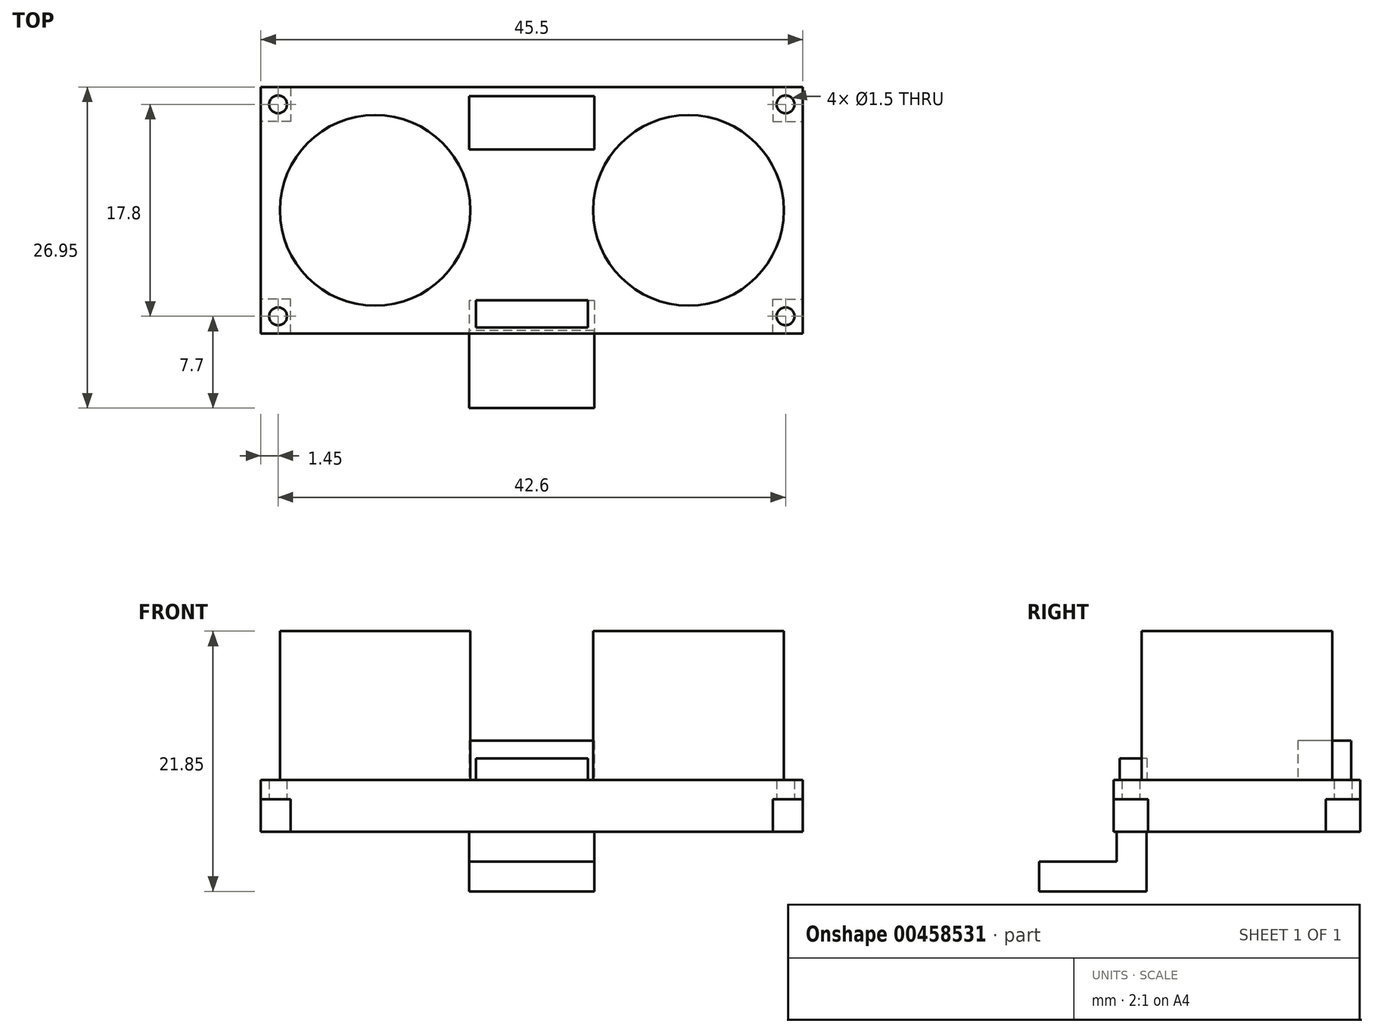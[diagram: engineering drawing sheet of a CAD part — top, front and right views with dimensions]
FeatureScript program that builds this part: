
annotation { "Feature Type Name" : "Feature", "Feature Type Description" : "" }
export const myFeature = defineFeature(function(context is Context, id is Id, definition is map)
    precondition{}
    {
        {
            var Q0;
            Q0=qCreatedBy(makeId("Top.planeOp"),FACE);
            var sketch = newSketch(context, id + "F0", { "sketchPlane" : qUnion([Q0])});
            skLineSegment(sketch, "E0.bottom", {"start": v(-22.75, 10.35) * mm, "end": v(22.75, 10.35) * mm});
            skLineSegment(sketch, "E0.top", {"start": v(-22.75, -10.35) * mm, "end": v(22.75, -10.35) * mm});
            skLineSegment(sketch, "E0.left", {"start": v(-22.75, 10.35) * mm, "end": v(-22.75, -10.35) * mm});
            skLineSegment(sketch, "E0.right", {"start": v(22.75, 10.35) * mm, "end": v(22.75, -10.35) * mm});
            skPoint(sketch, "E0.middle", {"position": v(0, 0) * mm});
            skCircle(sketch, "E1", {"center": v(-21.3, 8.9) * mm, "radius": 0.75 * mm});
            skCircle(sketch, "E2.MirrorC", {"center": v(21.3, 8.9) * mm, "radius": 0.75 * mm});
            skCircle(sketch, "E3.MirrorC", {"center": v(21.3, -8.9) * mm, "radius": 0.75 * mm});
            skCircle(sketch, "E4.MirrorC", {"center": v(-21.3, -8.9) * mm, "radius": 0.75 * mm});
            skSolve(sketch);
        }
        {
            var Q0;
            Q0=qSketchRegion(id+"F0",true);
            extrude(context, id + "F1", {"entities" : qUnion([Q0]), "depth" : 1.6 * mm});
        }
        {
            var Q0;
            Q0=makeQuery(id+"F1.opExtrude","CAP_FACE",FACE,{"disambiguationData":[OSD([sQuery(id+"F0.wireOp",EDGE,"E0.bottom"),sQuery(id+"F0.wireOp",EDGE,"E0.top"),sQuery(id+"F0.wireOp",EDGE,"E0.left"),sQuery(id+"F0.wireOp",EDGE,"E0.right"),sQuery(id+"F0.wireOp",EDGE,"E1"),sQuery(id+"F0.wireOp",EDGE,"E2.MirrorC"),sQuery(id+"F0.wireOp",EDGE,"E3.MirrorC"),sQuery(id+"F0.wireOp",EDGE,"E4.MirrorC"),sQuery(id+"F0.wireOp",EDGE,"EcKcbucg-EIJj-1O6K-RH2d-xdvmN5E1ucRb"),sQuery(id+"F0.wireOp",EDGE,"HiSo9sqT-VgG6-14Ua-RjyV-KtrsNFatjuRK")])],"isStart":false});
            var sketch = newSketch(context, id + "F2", { "sketchPlane" : qUnion([Q0])});
            skCircle(sketch, "E5", {"center": v(-13.15, 0) * mm, "radius": 8 * mm});
            skCircle(sketch, "E6", {"center": v(13.15, 0) * mm, "radius": 8 * mm});
            skLineSegment(sketch, "E7.bottom", {"start": v(-5.25, 9.6) * mm, "end": v(5.25, 9.6) * mm});
            skLineSegment(sketch, "E7.top", {"start": v(-5.25, 5.1) * mm, "end": v(5.25, 5.1) * mm});
            skLineSegment(sketch, "E7.left", {"start": v(-5.25, 9.6) * mm, "end": v(-5.25, 5.1) * mm});
            skLineSegment(sketch, "E7.right", {"start": v(5.25, 9.6) * mm, "end": v(5.25, 5.1) * mm});
            skPoint(sketch, "E7.middle", {"position": v(0, 7.35) * mm});
            skLineSegment(sketch, "E8.bottom", {"start": v(-4.7, -7.55) * mm, "end": v(4.7, -7.55) * mm});
            skLineSegment(sketch, "E8.top", {"start": v(-4.7, -9.85) * mm, "end": v(4.7, -9.85) * mm});
            skLineSegment(sketch, "E8.left", {"start": v(-4.7, -7.55) * mm, "end": v(-4.7, -9.85) * mm});
            skLineSegment(sketch, "E8.right", {"start": v(4.7, -7.55) * mm, "end": v(4.7, -9.85) * mm});
            skPoint(sketch, "E8.middle", {"position": v(0, -8.7) * mm});
            skSolve(sketch);
        }
        {
            var Q0;
            Q0=makeQuery(id+"F2.imprint","IMPRINT",FACE,{"disambiguationData":[TD([[makeQuery(id+"F2.imprint","IMPRINT",EDGE,{"derivedFrom":sQuery(id+"F2.wireOp",EDGE,"E5")}),1.0]])]});
            var Q1;
            Q1=makeQuery(id+"F2.imprint","IMPRINT",FACE,{"disambiguationData":[TD([[makeQuery(id+"F2.imprint","IMPRINT",EDGE,{"derivedFrom":sQuery(id+"F2.wireOp",EDGE,"E6")}),1.0]])]});
            extrude(context, id + "F3", {"entities" : qUnion([Q0, Q1]), "operationType" : NewBodyOperationType.ADD, "depth" : 12.5 * mm});
        }
        {
            var Q0;
            Q0=makeQuery(id+"F2.imprint","IMPRINT",FACE,{"disambiguationData":[TD([[makeQuery(id+"F2.imprint","IMPRINT",EDGE,{"derivedFrom":sQuery(id+"F2.wireOp",EDGE,"E7.bottom")}),-1.0]])]});
            extrude(context, id + "F4", {"entities" : qUnion([Q0]), "operationType" : NewBodyOperationType.ADD, "depth" : 3.3 * mm});
        }
        {
            var Q0;
            Q0=makeQuery(id+"F2.imprint","IMPRINT",FACE,{"disambiguationData":[TD([[makeQuery(id+"F2.imprint","IMPRINT",EDGE,{"derivedFrom":sQuery(id+"F2.wireOp",EDGE,"E8.bottom")}),-1.0]])]});
            extrude(context, id + "F5", {"entities" : qUnion([Q0]), "operationType" : NewBodyOperationType.ADD, "depth" : 1.8 * mm});
        }
        {
            var Q0;
            Q0=makeQuery(id+"F1.opExtrude","CAP_FACE",FACE,{"disambiguationData":[OSD([sQuery(id+"F0.wireOp",EDGE,"E0.bottom"),sQuery(id+"F0.wireOp",EDGE,"E0.top"),sQuery(id+"F0.wireOp",EDGE,"E0.left"),sQuery(id+"F0.wireOp",EDGE,"E0.right"),sQuery(id+"F0.wireOp",EDGE,"E1"),sQuery(id+"F0.wireOp",EDGE,"E2.MirrorC"),sQuery(id+"F0.wireOp",EDGE,"E3.MirrorC"),sQuery(id+"F0.wireOp",EDGE,"E4.MirrorC")])],"isStart":true});
            var sketch = newSketch(context, id + "F6", { "sketchPlane" : qUnion([Q0])});
            skLineSegment(sketch, "E9", {"start": v(-20.25, -10.35) * mm, "end": v(-20.25, -7.45) * mm});
            skLineSegment(sketch, "E10", {"start": v(-20.25, -7.45) * mm, "end": v(-22.75, -7.45) * mm});
            skLineSegment(sketch, "E11.MirrorCS", {"start": v(-20.25, 7.45) * mm, "end": v(-22.75, 7.45) * mm});
            skLineSegment(sketch, "E12.MirrorCS", {"start": v(-20.25, 10.35) * mm, "end": v(-20.25, 7.45) * mm});
            skLineSegment(sketch, "E13.MirrorCS", {"start": v(20.25, 10.35) * mm, "end": v(20.25, 7.45) * mm});
            skLineSegment(sketch, "E14.MirrorCS", {"start": v(20.25, 7.45) * mm, "end": v(22.75, 7.45) * mm});
            skLineSegment(sketch, "E15.MirrorCS", {"start": v(20.25, -10.35) * mm, "end": v(20.25, -7.45) * mm});
            skLineSegment(sketch, "E16.MirrorCS", {"start": v(20.25, -7.45) * mm, "end": v(22.75, -7.45) * mm});
            skSolve(sketch);
        }
        {
            var Q0;
            {var subQ6=sQuery(id+"F6.wireOp",EDGE,"E9");Q0=makeQuery(id+"F6.imprint","IMPRINT",FACE,{"disambiguationData":[TD([[makeQuery(id+"F6.imprint","IMPRINT",EDGE,{"derivedFrom":subQ6}),-1.0]])]});}
            extrude(context, id + "F7", {"entities" : qUnion([Q0]), "operationType" : NewBodyOperationType.ADD, "depth" : 2.75 * mm});
        }
        {
            var Q0;
            Q0=makeQuery(id+"F7.opExtrude","CAP_FACE",FACE,{"disambiguationData":[OSD([sQuery(id+"F0.wireOp",EDGE,"E0.bottom"),sQuery(id+"F0.wireOp",EDGE,"E0.top"),sQuery(id+"F0.wireOp",EDGE,"E0.left"),sQuery(id+"F0.wireOp",EDGE,"E0.right"),sQuery(id+"F6.wireOp",EDGE,"E9"),sQuery(id+"F6.wireOp",EDGE,"E10"),sQuery(id+"F6.wireOp",EDGE,"E11.MirrorCS"),sQuery(id+"F6.wireOp",EDGE,"E12.MirrorCS"),sQuery(id+"F6.wireOp",EDGE,"E13.MirrorCS"),sQuery(id+"F6.wireOp",EDGE,"E14.MirrorCS"),sQuery(id+"F6.wireOp",EDGE,"E15.MirrorCS"),sQuery(id+"F6.wireOp",EDGE,"E16.MirrorCS")])],"isStart":false});
            var sketch = newSketch(context, id + "F8", { "sketchPlane" : qUnion([Q0])});
            skLineSegment(sketch, "E17.bottom", {"start": v(5.25, 7.6) * mm, "end": v(-5.25, 7.6) * mm});
            skLineSegment(sketch, "E17.top", {"start": v(5.25, 10.1) * mm, "end": v(-5.25, 10.1) * mm});
            skLineSegment(sketch, "E17.left", {"start": v(5.25, 7.6) * mm, "end": v(5.25, 10.1) * mm});
            skLineSegment(sketch, "E17.right", {"start": v(-5.25, 7.6) * mm, "end": v(-5.25, 10.1) * mm});
            skSolve(sketch);
        }
        {
            var Q0;
            Q0=makeQuery(id+"F8.imprint","IMPRINT",FACE,{"disambiguationData":[TD([[makeQuery(id+"F8.imprint","IMPRINT",EDGE,{"derivedFrom":sQuery(id+"F8.wireOp",EDGE,"E17.bottom")}),-1.0]])]});
            extrude(context, id + "F9", {"entities" : qUnion([Q0]), "operationType" : NewBodyOperationType.ADD, "depth" : 5 * mm});
        }
        {
            var Q0;
            Q0=makeQuery(id+"F9.opExtrude","SWEPT_FACE",FACE,{"disambiguationData":[OSD([sQuery(id+"F8.wireOp",EDGE,"E17.top")])]});
            var sketch = newSketch(context, id + "F10", { "sketchPlane" : qUnion([Q0])});
            skLineSegment(sketch, "E18.bottom", {"start": v(-5.25, -7.75) * mm, "end": v(5.25, -7.75) * mm});
            skLineSegment(sketch, "E18.top", {"start": v(-5.25, -5.25) * mm, "end": v(5.25, -5.25) * mm});
            skLineSegment(sketch, "E18.left", {"start": v(-5.25, -7.75) * mm, "end": v(-5.25, -5.25) * mm});
            skLineSegment(sketch, "E18.right", {"start": v(5.25, -7.75) * mm, "end": v(5.25, -5.25) * mm});
            skSolve(sketch);
        }
        {
            var Q0;
            Q0=makeQuery(id+"F10.imprint","IMPRINT",FACE,{"disambiguationData":[TD([[makeQuery(id+"F10.imprint","IMPRINT",EDGE,{"derivedFrom":sQuery(id+"F10.wireOp",EDGE,"E18.bottom")}),-1.0]])]});
            extrude(context, id + "F11", {"entities" : qUnion([Q0]), "operationType" : NewBodyOperationType.ADD, "depth" : 6.5 * mm});
        }
    });
